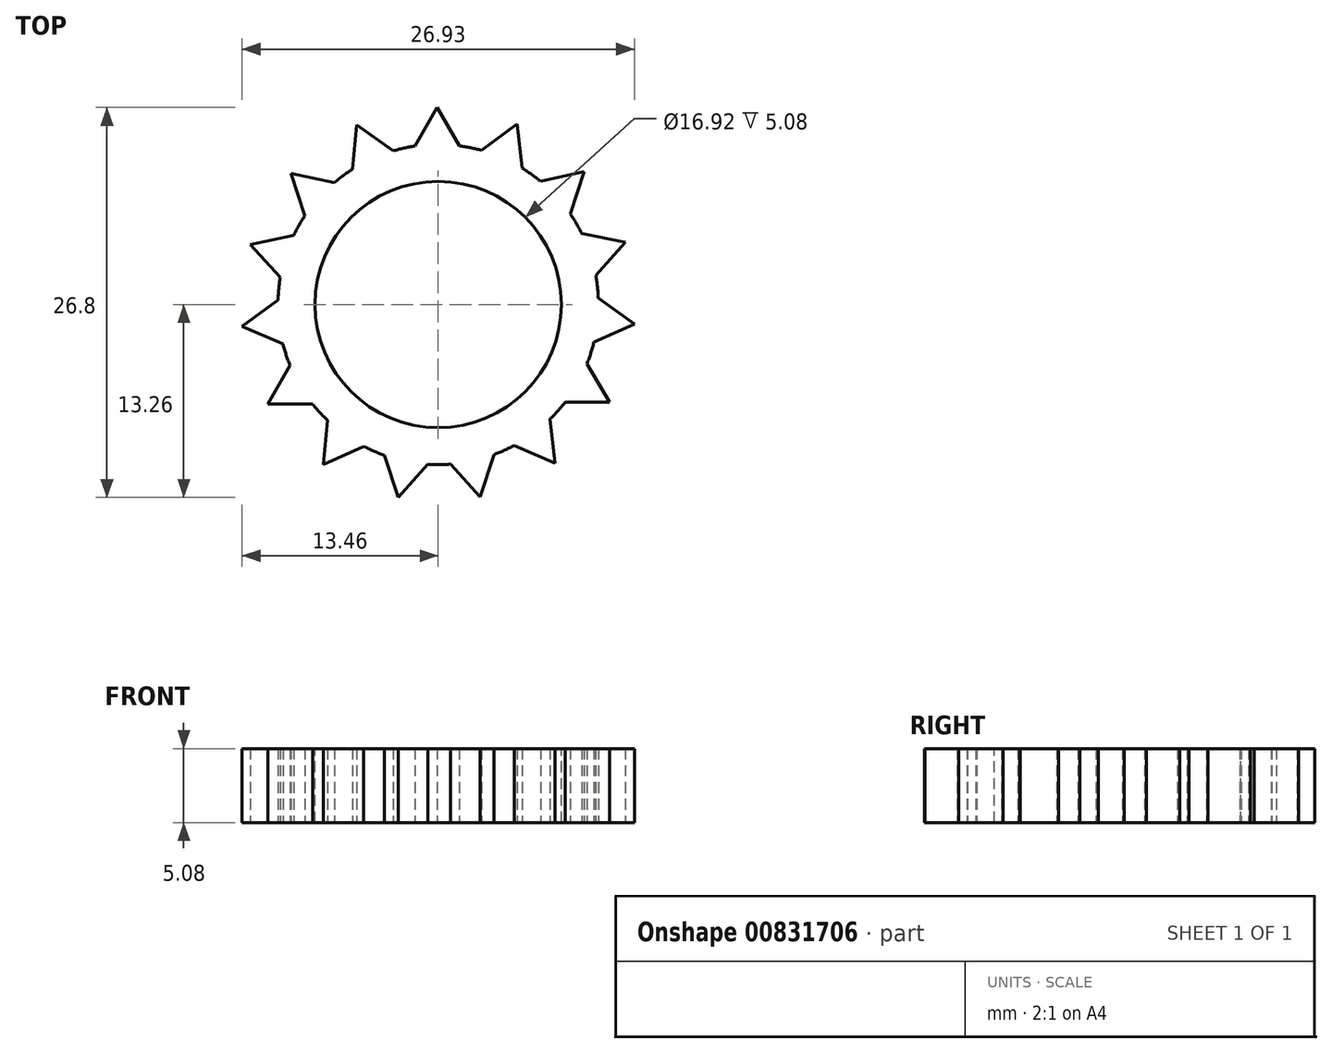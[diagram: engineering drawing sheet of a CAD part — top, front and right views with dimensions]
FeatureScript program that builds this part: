
annotation { "Feature Type Name" : "Feature", "Feature Type Description" : "" }
export const myFeature = defineFeature(function(context is Context, id is Id, definition is map)
    precondition{}
    {
        {
            var Q0;
            Q0=qCreatedBy(makeId("Top.planeOp"),FACE);
            var sketch = newSketch(context, id + "F0", { "sketchPlane" : qUnion([Q0])});
            skCircle(sketch, "E0", {"center": v(0, 0) * mm, "radius": 11 * mm});
            skPoint(sketch, "E1.0.midPoint", {"position": v(11.43, 6.7) * mm});
            skLineSegment(sketch, "E2", {"start": v(-5.58, 12.34) * mm, "end": v(-5.88, 9.3) * mm});
            skLineSegment(sketch, "E3", {"start": v(-7.9, -11) * mm, "end": v(-5.1, -9.74) * mm});
            skLineSegment(sketch, "E4", {"start": v(13.47, -1.33) * mm, "end": v(11, 0.45) * mm});
            skLineSegment(sketch, "E5", {"start": v(-10.12, 9) * mm, "end": v(-9.15, 6.1) * mm});
            skLineSegment(sketch, "E6", {"start": v(-2.74, -13.26) * mm, "end": v(-0.7, -10.98) * mm});
            skLineSegment(sketch, "E7", {"start": v(12.85, 4.26) * mm, "end": v(9.86, 4.88) * mm});
            skLineSegment(sketch, "E8", {"start": v(-12.9, 4.1) * mm, "end": v(-10.84, 1.85) * mm});
            skLineSegment(sketch, "E9", {"start": v(2.9, -13.23) * mm, "end": v(3.82, -10.31) * mm});
            skLineSegment(sketch, "E10", {"start": v(10, 9.12) * mm, "end": v(7.02, 8.47) * mm});
            skLineSegment(sketch, "E11", {"start": v(-13.46, -1.5) * mm, "end": v(-10.66, -2.72) * mm});
            skLineSegment(sketch, "E12", {"start": v(8.02, -10.9) * mm, "end": v(7.69, -7.87) * mm});
            skLineSegment(sketch, "E13", {"start": v(5.43, 12.4) * mm, "end": v(2.97, 10.6) * mm});
            skLineSegment(sketch, "E14", {"start": v(-11.68, -6.84) * mm, "end": v(-8.63, -6.82) * mm});
            skLineSegment(sketch, "E15", {"start": v(11.77, -6.7) * mm, "end": v(10.22, -4.06) * mm});
            skLineSegment(sketch, "E16", {"start": v(-0.08, 13.54) * mm, "end": v(-1.6, 10.88) * mm});
            skLineSegment(sketch, "E17.trimOffspring", {"start": v(-9.92, 4.76) * mm, "end": v(-12.9, 4.1) * mm});
            skLineSegment(sketch, "E18.trimOffspring", {"start": v(-7.6, -7.96) * mm, "end": v(-7.9, -11) * mm});
            skLineSegment(sketch, "E19.trimOffspring", {"start": v(-7.12, 8.38) * mm, "end": v(-10.12, 9) * mm});
            skLineSegment(sketch, "E20.trimOffspring", {"start": v(-10.17, -4.18) * mm, "end": v(-11.68, -6.84) * mm});
            skLineSegment(sketch, "E21.trimOffspring", {"start": v(-11, 0.31) * mm, "end": v(-13.46, -1.5) * mm});
            skLineSegment(sketch, "E22.trimOffspring", {"start": v(-3.1, 10.55) * mm, "end": v(-5.58, 12.34) * mm});
            skLineSegment(sketch, "E23.trimOffspring", {"start": v(1.46, 10.9) * mm, "end": v(-0.08, 13.54) * mm});
            skLineSegment(sketch, "E24.trimOffspring", {"start": v(5.77, 9.37) * mm, "end": v(5.43, 12.4) * mm});
            skLineSegment(sketch, "E25.trimOffspring", {"start": v(9.08, 6.2) * mm, "end": v(10, 9.12) * mm});
            skLineSegment(sketch, "E26.trimOffspring", {"start": v(10.82, 1.98) * mm, "end": v(12.85, 4.26) * mm});
            skLineSegment(sketch, "E27.trimOffspring", {"start": v(10.69, -2.6) * mm, "end": v(13.47, -1.33) * mm});
            skLineSegment(sketch, "E28.trimOffspring", {"start": v(8.71, -6.72) * mm, "end": v(11.77, -6.7) * mm});
            skLineSegment(sketch, "E29.trimOffspring", {"start": v(5.23, -9.68) * mm, "end": v(8.02, -10.9) * mm});
            skLineSegment(sketch, "E30.trimOffspring", {"start": v(0.84, -10.97) * mm, "end": v(2.9, -13.23) * mm});
            skLineSegment(sketch, "E31.trimOffspring", {"start": v(-3.7, -10.36) * mm, "end": v(-2.74, -13.26) * mm});
            skSolve(sketch);
        }
        {
            var Q0;
            Q0 = qSketchRegion(id + "F0", true);
            extrude(context, id + "F1", {"entities" : qUnion([Q0]), "depth" : 5.08 * mm, "offsetDistance" : 25.4 * mm});
        }
        {
            var Q0;
            Q0=makeQuery(id+"F1.opExtrude","CAP_FACE",FACE,{"disambiguationData":[OSD([sQuery(id+"F0.wireOp",EDGE,"E0"),sQuery(id+"F0.wireOp",EDGE,"E2"),sQuery(id+"F0.wireOp",EDGE,"E3"),sQuery(id+"F0.wireOp",EDGE,"E4"),sQuery(id+"F0.wireOp",EDGE,"E5"),sQuery(id+"F0.wireOp",EDGE,"E6"),sQuery(id+"F0.wireOp",EDGE,"E7"),sQuery(id+"F0.wireOp",EDGE,"E8"),sQuery(id+"F0.wireOp",EDGE,"E9"),sQuery(id+"F0.wireOp",EDGE,"E10"),sQuery(id+"F0.wireOp",EDGE,"E11"),sQuery(id+"F0.wireOp",EDGE,"E12"),sQuery(id+"F0.wireOp",EDGE,"E13"),sQuery(id+"F0.wireOp",EDGE,"E14"),sQuery(id+"F0.wireOp",EDGE,"E15"),sQuery(id+"F0.wireOp",EDGE,"E16"),sQuery(id+"F0.wireOp",EDGE,"E17.trimOffspring"),sQuery(id+"F0.wireOp",EDGE,"E18.trimOffspring"),sQuery(id+"F0.wireOp",EDGE,"E19.trimOffspring"),sQuery(id+"F0.wireOp",EDGE,"E20.trimOffspring"),sQuery(id+"F0.wireOp",EDGE,"E21.trimOffspring"),sQuery(id+"F0.wireOp",EDGE,"E22.trimOffspring"),sQuery(id+"F0.wireOp",EDGE,"E23.trimOffspring"),sQuery(id+"F0.wireOp",EDGE,"E24.trimOffspring"),sQuery(id+"F0.wireOp",EDGE,"E25.trimOffspring"),sQuery(id+"F0.wireOp",EDGE,"E26.trimOffspring"),sQuery(id+"F0.wireOp",EDGE,"E27.trimOffspring"),sQuery(id+"F0.wireOp",EDGE,"E28.trimOffspring"),sQuery(id+"F0.wireOp",EDGE,"E29.trimOffspring"),sQuery(id+"F0.wireOp",EDGE,"E30.trimOffspring"),sQuery(id+"F0.wireOp",EDGE,"E31.trimOffspring")])],"isStart":false});
            var sketch = newSketch(context, id + "F2", { "sketchPlane" : qUnion([Q0])});
            skCircle(sketch, "E32", {"center": v(0, 0) * mm, "radius": 8.46 * mm});
            skSolve(sketch);
        }
        {
            var Q0;
            Q0 = qSketchRegion(id + "F2", true);
            extrude(context, id + "F3", {"entities" : qUnion([Q0]), "operationType" : NewBodyOperationType.REMOVE, "oppositeDirection" : true, "depth" : 25.4 * mm, "offsetDistance" : 25.4 * mm});
        }
    });
